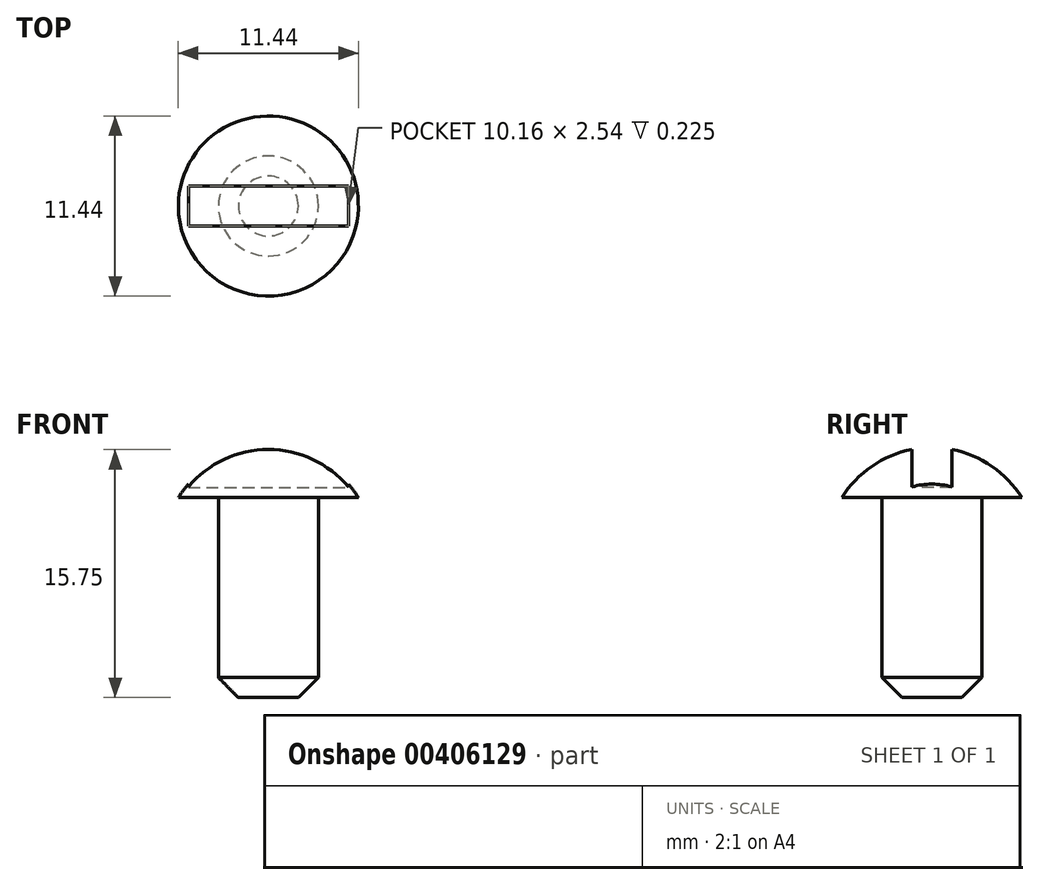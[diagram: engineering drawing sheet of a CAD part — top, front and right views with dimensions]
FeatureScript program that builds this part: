
annotation { "Feature Type Name" : "Feature", "Feature Type Description" : "" }
export const myFeature = defineFeature(function(context is Context, id is Id, definition is map)
    precondition{}
    {
        {
            var Q0;
            Q0=qCreatedBy(makeId("Front.planeOp"),FACE);
            var sketch = newSketch(context, id + "F0", { "sketchPlane" : qUnion([Q0])});
            skLineSegment(sketch, "E0", {"start": v(0, 0) * mm, "end": v(0, 15.88) * mm});
            skLineSegment(sketch, "E1", {"start": v(0, 0) * mm, "end": v(3.18, 0) * mm});
            skLineSegment(sketch, "E2", {"start": v(3.18, 0) * mm, "end": v(3.18, 12.7) * mm});
            skLineSegment(sketch, "E3", {"start": v(3.17, 12.7) * mm, "end": v(5.71, 12.7) * mm});
            skLineSegment(sketch, "E4", {"start": v(0, 0) * mm, "end": v(0, -4.07) * mm, "construction": true});
            skArc(sketch, "E5", {"start": v(5.71, 12.7) * mm, "mid": v(3.27, 15.03) * mm, "end": v(0, 15.88) * mm});
            skSolve(sketch);
        }
        {
            var Q0;
            Q0=makeQuery(id+"F0.imprint","IMPRINT",FACE,{"disambiguationData":[TD([[makeQuery(id+"F0.imprint","IMPRINT",EDGE,{"derivedFrom":sQuery(id+"F0.wireOp",EDGE,"E0")}),-1.0]])]});
            var Q1;
            Q1=sQuery(id+"F0.wireOp",EDGE,"E0");
            revolve(context, id + "F1", {"entities" : qUnion([Q0]), "axis" : qUnion([Q1]), "revolveType" : RevolveType.FULL});
        }
        {
            var Q0;
            Q0=makeQuery(id+"F1.opRevolve","SWEPT_FACE",FACE,{"disambiguationData":[OSD([sQuery(id+"F0.wireOp",EDGE,"E3")])]});
            cPlane(context, id + "F2", {"entities" : qUnion([Q0]), "cplaneType" : CPlaneType.OFFSET, "offset" : 0.64 * mm, "oppositeDirection" : true, "width" : 152.4 * mm, "height" : 152.4 * mm});
        }
        {
            var Q0;
            Q0=qCreatedBy(id+"F2.planeOp",FACE);
            var sketch = newSketch(context, id + "F3", { "sketchPlane" : qUnion([Q0])});
            skLineSegment(sketch, "E6.bottom", {"start": v(-5.08, -1.27) * mm, "end": v(5.08, -1.27) * mm});
            skLineSegment(sketch, "E6.top", {"start": v(-5.08, 1.27) * mm, "end": v(5.08, 1.27) * mm});
            skLineSegment(sketch, "E6.left", {"start": v(-5.08, -1.27) * mm, "end": v(-5.08, 1.27) * mm});
            skLineSegment(sketch, "E6.right", {"start": v(5.08, -1.27) * mm, "end": v(5.08, 1.27) * mm});
            skPoint(sketch, "E6.middle", {"position": v(0, 0) * mm});
            skSolve(sketch);
        }
        {
            var Q0;
            Q0=makeQuery(id+"F3.imprint","IMPRINT",FACE,{"disambiguationData":[TD([[makeQuery(id+"F3.imprint","IMPRINT",EDGE,{"derivedFrom":sQuery(id+"F3.wireOp",EDGE,"E6.bottom")}),1.0]])]});
            extrude(context, id + "F4", {"entities" : qUnion([Q0]), "operationType" : NewBodyOperationType.REMOVE, "endBound" : BoundingType.THROUGH_ALL, "oppositeDirection" : true, "depth" : 25.4 * mm});
        }
        {
            var Q0;
            Q0=makeQuery(id+"F1.opRevolve","SWEPT_EDGE",EDGE,{"disambiguationData":[OSD([sQuery(id+"F0.wireOp",EDGE,"E1"),sQuery(id+"F0.wireOp",EDGE,"E2")])]});
            chamfer(context, id + "F5", {"entities" : qUnion([Q0]), "width" : 1.27 * mm, "tangentPropagation" : true});
        }
    });
